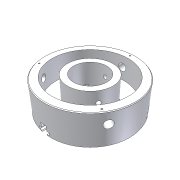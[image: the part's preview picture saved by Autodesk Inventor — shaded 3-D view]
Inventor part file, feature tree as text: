
AUTODESK INVENTOR PART (.ipt)
format: ipt  version: unknown  size: 333,824 bytes
history: native  units: in
note: dims shown in document units (in); Inventor stores cm internally (conversion verified against a paired STEP export)
features: sketch x5, extrude x4, plane x2, revolve x1, other x1, pattern_circular x1, chamfer x1, projected_geometry x1, reference x1
ambient origin geometry x8: Origin, YZ Plane, XZ Plane, XY Plane, X Axis, Y Axis, Z Axis, Center Point
feature tree (17):
  revolve  "Revolution3"  [1 undecoded]
  extrude  "Extrusion8"  Depth=0.1969in
  plane  "Work Plane1"
  extrude  "Extrusion12"  Depth=0.5906in
  extrude  "Extrusion13"  Depth=0.0787in
  plane  "Work Plane2"
  other  "Work Axis2"
  extrude  "Extrusion14"  Depth=0.1378in
  pattern_circular  "Circular Pattern1"  [2 undecoded]
  chamfer  "Chamfer1"  Distance=0.0394in
  sketch  "Sketch10"  dims[d51=0.5906in d52=0.1575in]
  sketch  "Sketch11"  dims[d53=0.9843in d54=0.1969in]
  projected_geometry  "Projected Loop1"
  sketch  "Sketch15"  dims[d55=0.1969in d56=0.5906in]
  reference  "Reference2"
  sketch  "Sketch16"  dims[d58=90.0deg d60=0.0787in]
  sketch  "Sketch17"  dims[d61=0.0787in d62=0.1378in d63=0.0787in d64=0.0394in d65=0.3937in d66=0.0in d67=0.0in d68=0.0787in d69=0.0in d72=-1.378in d78=0.3937in d79=0.0in d80=0.3937in d81=0.0in d82=-1.1811in d83=0.1969in d84=0.3937in d85=0.0in d86=0.0394in d87=1.1811in d88=360.0deg d90=0.0157in d91=0.0787in d92=45.0deg]
note: 3 required parameter values undecoded (feature->parameter linkage not recoverable at this tier; creation-order binding heuristic only, values carry confidence <= 0.55)